# Revit family: Construction_Other_Sjobergs_Planing_Machine
name_source: partatom
category: Specialty Equipment
revit_build: Autodesk Revit 2017 (Build: 20190508_0315(x64)
units: mm (PartAtom-declared; Revit-internal decimal feet)

## family parameters
Always vertical = Yes
Cut with Voids When Loaded = No
OmniClass Number = 23.45.30.14.11
OmniClass Title = Commercial Dishwashers
Part Type = Normal
Room Calculation Point = No
Round Connector Dimension = Use Diameter
Shared = No
Work Plane-Based = No

## types (1)
- 37000 EJCA Planing machine L38 / 310
    AssetType = Movable
    BIMObjectName = Construction_Other_Sjobergs_Planing_Machine
    Brand = EJCA
    Category = Machines
    Color = Green
    Constituents = The standard equipment includes planer HSS, folding straight planer stop, steel setting template, motor protection with zero voltage release, automatic brake and emergency stop. The machine can be equipped w/ indexable cutter.
    ConvergoRefNr = 0184-2005-0023-SE
    Cost = 0 $
    CuttingDepthPlaner = 6/5 mm
    DurationUnit = Year
    ElectricalDeviceNominalPower = 2200 W
    Features = The planer tables are easily adjustable and can be adjusted very easily with a lever. Installed lifting aids in the form of a gas spring. The planer tables are regulated with a crank in a comfortable working position.CE-standard.
    FeedSpeed = 6 m / min
    Finish = Cast iron
    HasProtectiveEarth = Yes
    HoseConnection = 100 mm
    IfcExportAs = IfcFurnishingElementType
    IfcExportType = TABLE
    MachineryMainMaterial = Green metal
    MachineryQuaternaryMaterial = Clearance
    MachinerySecondaryMaterial = Black Metal
    MachineryTertiaryMaterial = Stainless Steel
    Manufacturer = Sjöbergs
    ManufacturerName = Sjöbergs
    ManufacturerURL = https://www.sjobergs.se
    Material = Metal, plastic
    Model = 37000 EJCA Planing machine L38 / 310
    ModelReference = 37000
    NBSDescription = School art, design and technology tables and workbenches;
    NBSReference = 45-35-20/320
    Name = Sjobergs_Planing_Machine
    NominalCurrent = 0 A
    NominalDepth = 595 mm  [stored 1.9521 ft]
    NominalFrequencyRange = 0 Hz
    NominalHeight = 1020 mm
    NominalVoltage = 230 V
    NominalWidth = 1500 mm
    NumberOfPoles = 0
    NumberPlanerSteels = 3 pcs
    PhaseAngle = 0.00°
    PlanerSizes = Planer table L 670 mm. Planer width W 310 mm. Planer height 235 mm. Working Height 870 mm.
    PlannerCutter = Ø 80 mm
    ProductDatasheet = https://www.sjobergs.se
    ProductInformation = Made in Sweden of the best quality, long service life.The tables are made of cast iron and planed, which gives an unsurpassed feeling and low friction.The planer tables are easily adjustable and can be adjusted w/ a lever.
    Shape = Sculptured
    Size = 1500x595x1020 mm
    SpeedPlanerCutter = 5500 rpm
    URL = https://www.sjobergs.se
    Uniclass2 = Pr_40_50_21
    Uniclass2015Description = Desks, Tables And Worktops
    Uniclass2015Reference = Pr_40_50_21_76
    UsageCurrent = 0 A
    Version = 1
    VersionDate = 01/07/2020
    WarrantyDurationUnit = Year
    Weight = 295.0 kg

note: [stored X ft] marks values corroborated as IEEE doubles in the binary element streams (Revit-internal decimal feet)

## geometry (parser evidence)
native form markers: Sweep x4
no freeform markers — native parametric forms only
